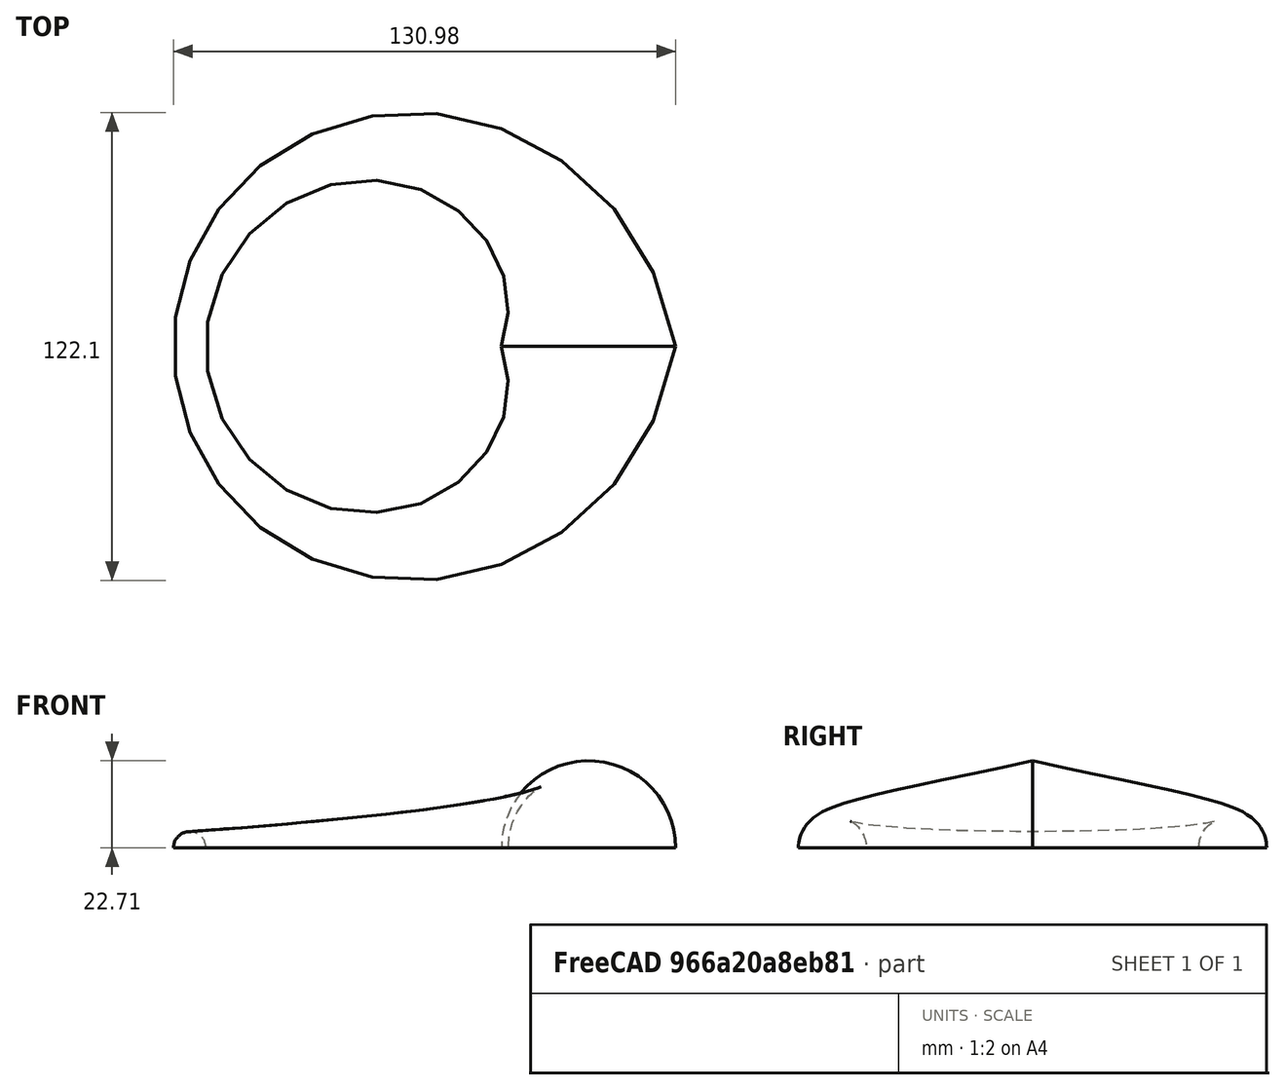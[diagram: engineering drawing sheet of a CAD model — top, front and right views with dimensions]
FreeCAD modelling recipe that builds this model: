
FCSTD DOCUMENT  (FreeCAD 0.21R33771 (Git))
Label: plavnijPerehod
License: All rights reserved
LicenseURL: http://en.wikipedia.org/wiki/All_rights_reserved
objects: Sketcher::SketchObject×3, PartDesign::Body×1, Part::Sweep×1
note: 5 computed .brp shape members not serialized (recipe doc carries the construction recipe); baked Part::Feature solids carry a one-line shape summary decoded from their .brp

FEATURE [Sketcher::SketchObject] Sketch
  FullyConstrained = false
  MapMode = 5
  Placement = pos=(0,0,0) rot=(1,0,0;1.5708rad)
  Support = -> [XZ_Plane]
  sketch-geometry (2):
    g0: ArcOfCircle CenterX=-76.6724 CenterY=0 CenterZ=0 NormalX=0 NormalY=0 NormalZ=1 AngleXU=0 Radius=4.23346 StartAngle=0 EndAngle=3.14159
    g1: LineSegment StartX=-80.9059 StartY=5e-16 StartZ=0 EndX=-72.439 EndY=0 EndZ=0
  constraints (4):
    c: PointOnObject(g0,g-1)
    c: Coincident(g0,g1)
    c: Coincident(g0,g1)
    c: Tangent(g1,g-1)
FEATURE [Sketcher::SketchObject] Sketch001
  FullyConstrained = false
  MapMode = 5
  Placement = pos=(0,0,0) rot=(1,0,0;1.5708rad)
  Support = -> [XZ_Plane]
  sketch-geometry (2):
    g0: ArcOfCircle CenterX=27.352 CenterY=0 CenterZ=0 NormalX=0 NormalY=0 NormalZ=1 AngleXU=0 Radius=22.715 StartAngle=0 EndAngle=3.14159
    g1: LineSegment StartX=4.63706 StartY=2.8e-15 StartZ=0 EndX=50.067 EndY=0 EndZ=0
  constraints (4):
    c: PointOnObject(g0,g-1)
    c: Coincident(g0,g1)
    c: Coincident(g0,g1)
    c: Tangent(g1,g-1)
FEATURE [Sketcher::SketchObject] Sketch002
  FullyConstrained = false
  MapMode = 5
  Support = -> [XY_Plane]
  sketch-geometry (1):
    g0: Circle CenterX=-24.9307 CenterY=0 CenterZ=0 NormalX=0 NormalY=0 NormalZ=1 AngleXU=0 Radius=51.7887
  constraints (1):
    c: PointOnObject(g0,g-1)
FEATURE [PartDesign::Body] Body
  Group = -> [Sketch,Sketch001,Sketch002]
  Origin = -> Origin
FEATURE [Part::Sweep] Sweep
  Frenet = true
  Sections = -> [Sketch,Sketch001]
  Solid = true
  Spine = -> Sketch002 [Edge1]
  Transition = 1
